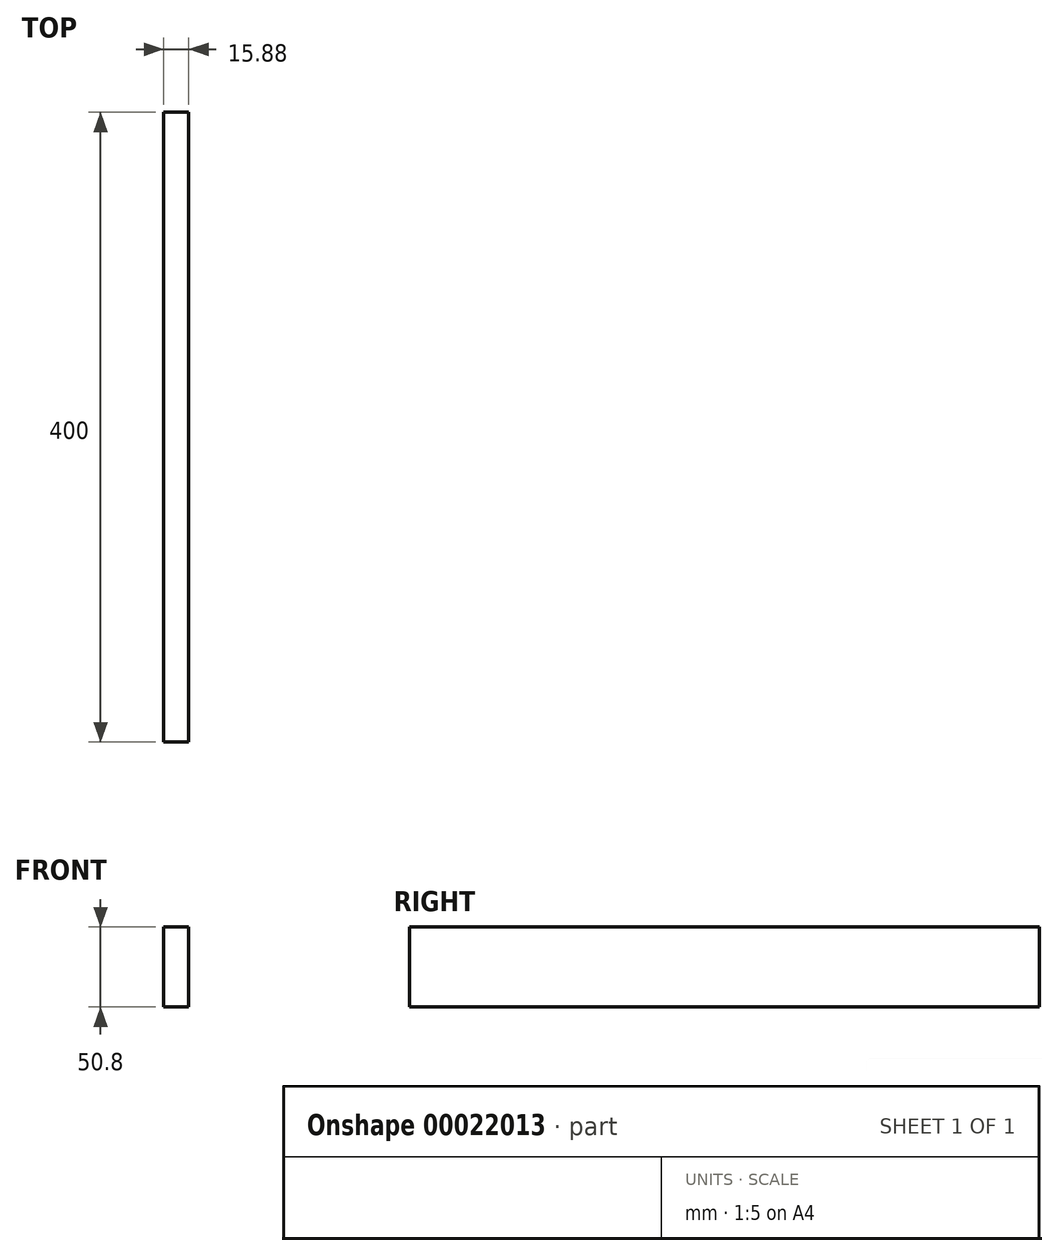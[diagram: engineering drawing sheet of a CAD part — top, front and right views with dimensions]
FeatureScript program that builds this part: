
annotation { "Feature Type Name" : "Feature", "Feature Type Description" : "" }
export const myFeature = defineFeature(function(context is Context, id is Id, definition is map)
    precondition{}
    {
        {
            var Q0;
            Q0=qCreatedBy(makeId("Top.planeOp"),FACE);
            var sketch = newSketch(context, id + "F0", { "sketchPlane" : qUnion([Q0])});
            skLineSegment(sketch, "E0.bottom", {"start": v(0, 0) * mm, "end": v(-15.88, 0) * mm});
            skLineSegment(sketch, "E0.top", {"start": v(0, -400) * mm, "end": v(-15.87, -400) * mm});
            skLineSegment(sketch, "E0.left", {"start": v(0, 0) * mm, "end": v(0, -400) * mm});
            skLineSegment(sketch, "E0.right", {"start": v(-15.88, 0) * mm, "end": v(-15.88, -400) * mm});
            skSolve(sketch);
        }
        {
            var Q0;
            Q0 = qSketchRegion(id + "F0", true);
            extrude(context, id + "F1", {"entities" : qUnion([Q0]), "depth" : 50.8 * mm});
        }
    });
